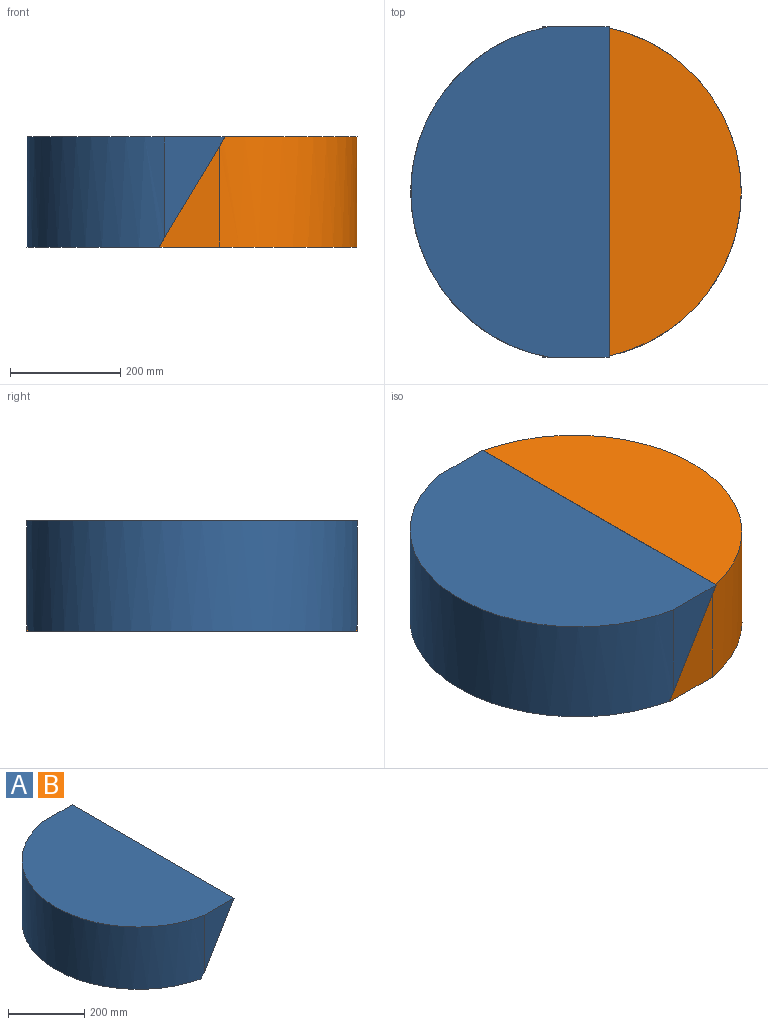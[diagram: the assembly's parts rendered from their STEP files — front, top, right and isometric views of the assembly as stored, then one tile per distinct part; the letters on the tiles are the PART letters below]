
ASSEMBLY  parts=2 mates=1
PART A: 6 faces, bbox 360x600x200 mm
  f0: plane 600x200mm, normal (0.86,0,-0.51), area 139905mm2, adj f1,f2,f3,f4,f5
  f1: plane 600x360mm, normal (0,0,1), area 178756.1mm2, adj f0,f3,f4,f5
  f2: plane 595.99x240mm, normal (0,0,-1), area 106775.5mm2, adj f0,f5
  f3: plane 183.33x110mm, normal (0,-1,0), area 10083.3mm2, adj f0,f1,f5
  f4: plane 183.33x110mm, normal (0,1,0), area 10083.3mm2, adj f0,f1,f5
  f5: cylinder r=305mm len=600mm, axis (0,0,1), area 169346.3mm2, adj f0,f1,f2,f3,f4
PART B: same geometry as A
PLACE A t=(-430.02,42.18,-66.66)mm
PLACE B rot(axis=(0,1,0),180deg) t=(-309.99,42.18,133.39)mm
MATE fastened B.f0 <-> A.f0  axis (-0.86,0,0.51) through (-370.01,-257.82,33.37)mm
